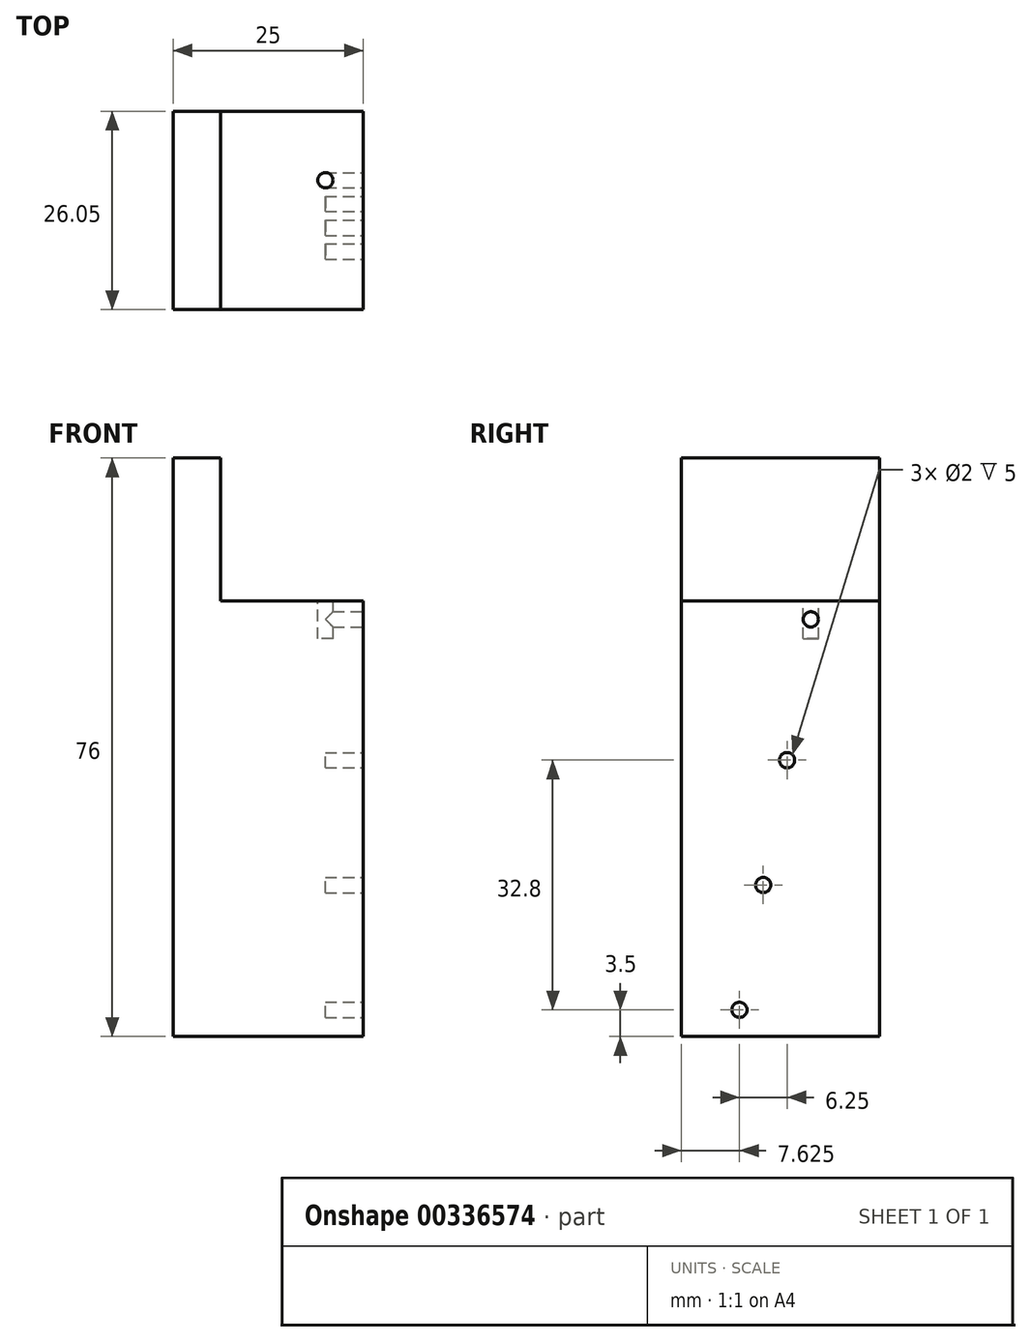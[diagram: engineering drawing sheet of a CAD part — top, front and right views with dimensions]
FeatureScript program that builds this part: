
annotation { "Feature Type Name" : "Feature", "Feature Type Description" : "" }
export const myFeature = defineFeature(function(context is Context, id is Id, definition is map)
    precondition{}
    {
        {
            var Q0;
            Q0=qCreatedBy(makeId("Front.planeOp"),FACE);
            var sketch = newSketch(context, id + "F0", { "sketchPlane" : qUnion([Q0])});
            skLineSegment(sketch, "E0", {"start": v(0, 0) * mm, "end": v(0, 76) * mm});
            skLineSegment(sketch, "E1", {"start": v(0, 76) * mm, "end": v(6.25, 76) * mm});
            skLineSegment(sketch, "E2", {"start": v(6.25, 76) * mm, "end": v(6.25, 57.25) * mm});
            skLineSegment(sketch, "E3", {"start": v(6.25, 57.25) * mm, "end": v(25, 57.25) * mm});
            skLineSegment(sketch, "E4", {"start": v(25, 57.25) * mm, "end": v(25, 0) * mm});
            skLineSegment(sketch, "E5", {"start": v(25, 0) * mm, "end": v(0, 0) * mm});
            skSolve(sketch);
        }
        {
            var Q0;
            Q0 = qSketchRegion(id + "F0", true);
            extrude(context, id + "F1", {"entities" : qUnion([Q0]), "oppositeDirection" : true, "depth" : 26.05 * mm});
        }
        {
            var Q0;
            Q0=makeQuery(id+"F1.opExtrude","SWEPT_FACE",FACE,{"disambiguationData":[OSD([sQuery(id+"F0.wireOp",EDGE,"E4")])]});
            var sketch = newSketch(context, id + "F2", { "sketchPlane" : qUnion([Q0])});
            skPoint(sketch, "E6.centerSnap0", {"position": v(13.03, 0) * mm});
            skLineSegment(sketch, "E7", {"start": v(7.63, 3.5) * mm, "end": v(7.63, 19.9) * mm, "construction": true});
            skLineSegment(sketch, "E8", {"start": v(7.63, 19.9) * mm, "end": v(10.75, 19.9) * mm, "construction": true});
            skLineSegment(sketch, "E9", {"start": v(10.75, 19.9) * mm, "end": v(10.75, 36.3) * mm, "construction": true});
            skLineSegment(sketch, "E10", {"start": v(10.75, 36.3) * mm, "end": v(13.88, 36.3) * mm, "construction": true});
            skLineSegment(sketch, "E11", {"start": v(13.88, 36.3) * mm, "end": v(13.88, 54.8) * mm, "construction": true});
            skLineSegment(sketch, "E12", {"start": v(13.88, 54.8) * mm, "end": v(17, 54.8) * mm, "construction": true});
            skCircle(sketch, "E13", {"center": v(7.63, 3.5) * mm, "radius": 1 * mm});
            skCircle(sketch, "E14", {"center": v(10.75, 19.9) * mm, "radius": 1 * mm});
            skCircle(sketch, "E15", {"center": v(13.88, 36.3) * mm, "radius": 1 * mm});
            skCircle(sketch, "E16", {"center": v(17, 54.8) * mm, "radius": 1 * mm});
            skSolve(sketch);
        }
        {
            var Q0;
            Q0=makeQuery(id+"F2.imprint","IMPRINT",FACE,{"disambiguationData":[TD([[makeQuery(id+"F2.imprint","IMPRINT",EDGE,{"derivedFrom":sQuery(id+"F2.wireOp",EDGE,"E16")}),1.0]])]});
            var Q1;
            Q1=makeQuery(id+"F2.imprint","IMPRINT",FACE,{"disambiguationData":[TD([[makeQuery(id+"F2.imprint","IMPRINT",EDGE,{"derivedFrom":sQuery(id+"F2.wireOp",EDGE,"E15")}),1.0]])]});
            var Q2;
            Q2=makeQuery(id+"F2.imprint","IMPRINT",FACE,{"disambiguationData":[TD([[makeQuery(id+"F2.imprint","IMPRINT",EDGE,{"derivedFrom":sQuery(id+"F2.wireOp",EDGE,"E14")}),1.0]])]});
            var Q3;
            Q3=makeQuery(id+"F2.imprint","IMPRINT",FACE,{"disambiguationData":[TD([[makeQuery(id+"F2.imprint","IMPRINT",EDGE,{"derivedFrom":sQuery(id+"F2.wireOp",EDGE,"E13")}),1.0]])]});
            var Q4;
            Q4=sQuery(id+"F2.wireOp",EDGE,"E16");
            var Q5;
            Q5=sQuery(id+"F2.wireOp",EDGE,"E15");
            var Q6;
            Q6=sQuery(id+"F2.wireOp",EDGE,"E14");
            var Q7;
            Q7=sQuery(id+"F2.wireOp",EDGE,"E13");
            extrude(context, id + "F3", {"entities" : qUnion([Q0, Q1, Q2, Q3]), "operationType" : NewBodyOperationType.REMOVE, "surfaceEntities" : qUnion([Q4, Q5, Q6, Q7]), "oppositeDirection" : true, "depth" : 5 * mm});
        }
        {
            var Q0;
            Q0=makeQuery(id+"F1.opExtrude","SWEPT_FACE",FACE,{"disambiguationData":[OSD([sQuery(id+"F0.wireOp",EDGE,"E3")])]});
            var sketch = newSketch(context, id + "F4", { "sketchPlane" : qUnion([Q0])});
            skCircle(sketch, "E17", {"center": v(20, 17) * mm, "radius": 1 * mm});
            skSolve(sketch);
        }
        {
            var Q0;
            Q0=makeQuery(id+"F4.imprint","IMPRINT",FACE,{"disambiguationData":[TD([[makeQuery(id+"F4.imprint","IMPRINT",EDGE,{"derivedFrom":sQuery(id+"F4.wireOp",EDGE,"E17")}),1.0]])]});
            var Q1;
            Q1=sQuery(id+"F4.wireOp",EDGE,"E17");
            extrude(context, id + "F5", {"entities" : qUnion([Q0]), "operationType" : NewBodyOperationType.REMOVE, "surfaceEntities" : qUnion([Q1]), "oppositeDirection" : true, "depth" : 5 * mm});
        }
    });
